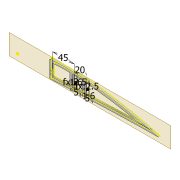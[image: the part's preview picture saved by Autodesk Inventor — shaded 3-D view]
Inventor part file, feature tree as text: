
AUTODESK INVENTOR PART (.ipt)
format: ipt  version: 2022 (Build 260153000, 153)  size: 325,632 bytes
history: native  units: mm
features: extrude x6, sketch x6, projected_geometry x4, shell x1, fillet x1, plane x1
ambient origin geometry x8: Origin, YZ Plane, XZ Plane, XY Plane, X Axis, Y Axis, Z Axis, Center Point
bodies: Solid1 (feature_tree)
feature tree (19):
  extrude  "Extrusion1"  Depth=5.0mm
  shell  "Shell1"  Thickness=6.0mm
  extrude  "Extrusion2"  Depth=2.0mm
  extrude  "Extrusion3"  Depth=5.9mm
  extrude  "Extrusion4"  Depth=10.0mm TaperAngle=0.0deg
  fillet  "Fillet1"  Radius=70.0mm
  plane  "Work Plane1"
  extrude  "Extrusion5"  Depth=4.0mm TaperAngle=0.0deg
  extrude  "Extrusion8"  Depth=0.5mm
  sketch  "Sketch3"  dims[d0=4.0mm d1=0.0mm d2=5.0mm d3=6.0mm]
  sketch  "Sketch7"  dims[d5=4.0mm d6=0.0mm d7=2.0mm]
  projected_geometry  "Projected Loop3"
  sketch  "Sketch8"  dims[d8=2.0mm d9=5.9mm]
  sketch  "Sketch9"  dims[d12=5.0mm d13=10.0mm d14=0.0mm d15=70.0mm]
  sketch  "Sketch10"  dims[d16=10.0mm d17=0.0mm d22=4.0mm d23=0.0mm]
  projected_geometry  "Projected Loop4"
  projected_geometry  "Projected Loop10"
  sketch  "Sketch16"  dims[d24=2.0mm d26=2.0mm d31=2.0mm d32=5.0mm d34=1.6mm d35=2.5mm d37=5.0mm d38=1.6mm d40=2.5mm d41=45.0mm d42=20.0mm d43=0.5mm d44=10.0mm d45=0.0mm]
  projected_geometry  "Projected Loop11"
